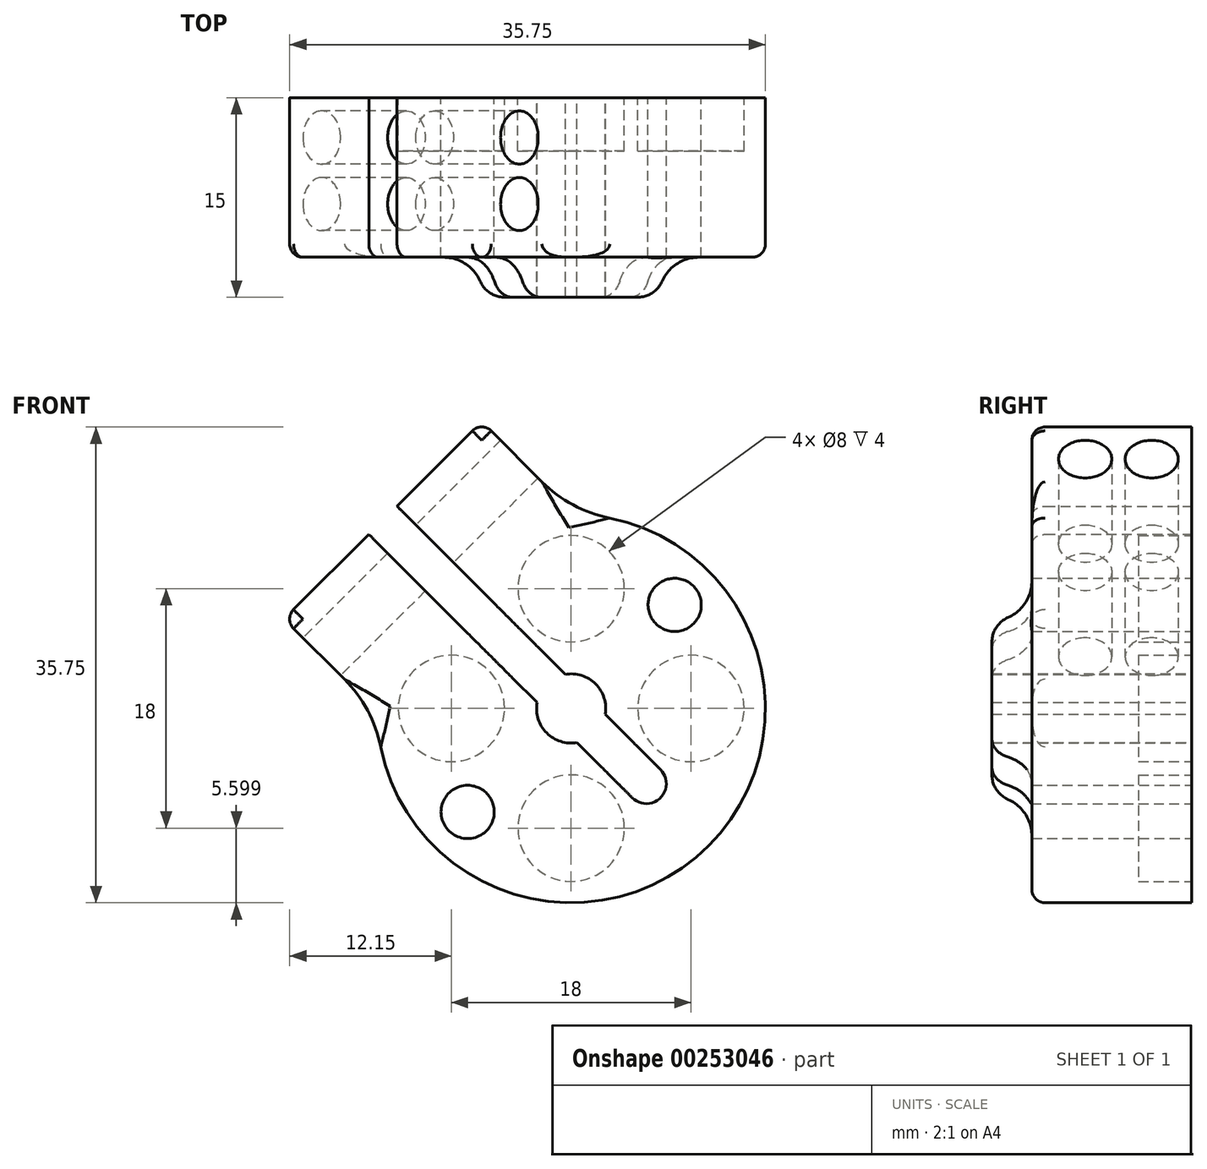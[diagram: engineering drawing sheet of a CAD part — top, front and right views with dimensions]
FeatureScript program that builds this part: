
annotation { "Feature Type Name" : "Feature", "Feature Type Description" : "" }
export const myFeature = defineFeature(function(context is Context, id is Id, definition is map)
    precondition{}
    {
        {
            var Q0;
            Q0=qCreatedBy(makeId("Right.planeOp"),FACE);
            var sketch = newSketch(context, id + "F0", { "sketchPlane" : qUnion([Q0])});
            skLineSegment(sketch, "E0", {"start": v(-60.78, -4.86) * mm, "end": v(-45.78, -4.86) * mm});
            skLineSegment(sketch, "E1", {"start": v(-45.78, -4.86) * mm, "end": v(-45.78, 7.14) * mm});
            skLineSegment(sketch, "E2", {"start": v(-45.78, 7.14) * mm, "end": v(-57.78, 7.14) * mm});
            skLineSegment(sketch, "E3", {"start": v(-57.78, 7.14) * mm, "end": v(-57.78, -0.46) * mm});
            skLineSegment(sketch, "E4", {"start": v(-57.78, -0.46) * mm, "end": v(-60.78, -0.46) * mm});
            skLineSegment(sketch, "E5", {"start": v(-60.78, -0.46) * mm, "end": v(-60.78, -4.86) * mm});
            skLineSegment(sketch, "E6", {"start": v(-43.04, -7.46) * mm, "end": v(-64.3, -7.46) * mm, "construction": true});
            skSolve(sketch);
        }
        {
            var Q0;
            Q0 = qSketchRegion(id + "F0", true);
            var Q1;
            Q1=sQuery(id+"F0.wireOp",EDGE,"E6");
            revolve(context, id + "F1", {"entities" : qUnion([Q0]), "axis" : qUnion([Q1]), "revolveType" : RevolveType.FULL});
        }
        {
            var Q0;
            Q0=makeQuery(id+"F1.opRevolve","SWEPT_EDGE",EDGE,{"disambiguationData":[OSD([sQuery(id+"F0.wireOp",EDGE,"E4"),sQuery(id+"F0.wireOp",EDGE,"E5")])]});
            fillet(context, id + "F2", {"entities" : qUnion([Q0]), "radius" : 2 * mm, "tangentPropagation" : true, "allowEdgeOverflow" : false});
        }
        {
            var Q0;
            Q0=makeQuery(id+"F1.opRevolve","SWEPT_FACE",FACE,{"disambiguationData":[OSD([sQuery(id+"F0.wireOp",EDGE,"E1")])]});
            var sketch = newSketch(context, id + "F3", { "sketchPlane" : qUnion([Q0])});
            skCircle(sketch, "E7", {"center": v(0, 1.54) * mm, "radius": 4 * mm});
            skPoint(sketch, "E8", {"position": v(0, -7.46) * mm});
            skCircle(sketch, "E9.1.0", {"center": v(-9, -7.46) * mm, "radius": 4 * mm});
            skCircle(sketch, "E9.2.0", {"center": v(0, -16.46) * mm, "radius": 4 * mm});
            skCircle(sketch, "E9.3.0", {"center": v(9, -7.46) * mm, "radius": 4 * mm});
            skSolve(sketch);
        }
        {
            var Q0;
            Q0=makeQuery(id+"F3.imprint","IMPRINT",FACE,{"disambiguationData":[TD([[makeQuery(id+"F3.imprint","IMPRINT",EDGE,{"derivedFrom":sQuery(id+"F3.wireOp",EDGE,"E7")}),1.0]])]});
            var Q1;
            Q1=makeQuery(id+"F3.imprint","IMPRINT",FACE,{"disambiguationData":[TD([[makeQuery(id+"F3.imprint","IMPRINT",EDGE,{"derivedFrom":sQuery(id+"F3.wireOp",EDGE,"E9.1.0")}),1.0]])]});
            var Q2;
            Q2=makeQuery(id+"F3.imprint","IMPRINT",FACE,{"disambiguationData":[TD([[makeQuery(id+"F3.imprint","IMPRINT",EDGE,{"derivedFrom":sQuery(id+"F3.wireOp",EDGE,"E9.2.0")}),1.0]])]});
            var Q3;
            Q3=makeQuery(id+"F3.imprint","IMPRINT",FACE,{"disambiguationData":[TD([[makeQuery(id+"F3.imprint","IMPRINT",EDGE,{"derivedFrom":sQuery(id+"F3.wireOp",EDGE,"E9.3.0")}),1.0]])]});
            extrude(context, id + "F4", {"entities" : qUnion([Q0, Q1, Q2, Q3]), "operationType" : NewBodyOperationType.REMOVE, "oppositeDirection" : true, "depth" : 4 * mm});
        }
        {
            var Q0;
            Q0=makeQuery(id+"F1.opRevolve","SWEPT_FACE",FACE,{"disambiguationData":[OSD([sQuery(id+"F0.wireOp",EDGE,"E1")])]});
            var sketch = newSketch(context, id + "F5", { "sketchPlane" : qUnion([Q0])});
            skLineSegment(sketch, "E10.0", {"start": v(0.35, -9.23) * mm, "end": v(18.03, 8.45) * mm});
            skLineSegment(sketch, "E11.0", {"start": v(-1.77, -7.1) * mm, "end": v(15.9, 10.57) * mm});
            skLineSegment(sketch, "E12", {"start": v(15.9, 10.57) * mm, "end": v(18.03, 8.45) * mm});
            skLineSegment(sketch, "E13", {"start": v(-1.77, -7.1) * mm, "end": v(0.35, -9.23) * mm});
            skPoint(sketch, "E14", {"position": v(0, -7.46) * mm});
            skSolve(sketch);
        }
        {
            var Q0;
            Q0 = qSketchRegion(id + "F5", true);
            extrude(context, id + "F6", {"entities" : qUnion([Q0]), "operationType" : NewBodyOperationType.REMOVE, "oppositeDirection" : true, "depth" : 25 * mm});
        }
        {
            var Q0;
            Q0=makeQuery(id+"F1.opRevolve","SWEPT_FACE",FACE,{"disambiguationData":[OSD([sQuery(id+"F0.wireOp",EDGE,"E1")])]});
            var sketch = newSketch(context, id + "F7", { "sketchPlane" : qUnion([Q0])});
            skPoint(sketch, "E15", {"position": v(0, -7.46) * mm});
            skLineSegment(sketch, "E16", {"start": v(8.3, 2.96) * mm, "end": v(13.08, 7.74) * mm});
            skLineSegment(sketch, "E17", {"start": v(13.08, 7.74) * mm, "end": v(6.72, 14.1) * mm});
            skLineSegment(sketch, "E18", {"start": v(6.72, 14.1) * mm, "end": v(-0.25, 7.14) * mm});
            skLineSegment(sketch, "E19", {"start": v(0, -7.46) * mm, "end": v(12.08, 4.61) * mm, "construction": true});
            skLineSegment(sketch, "E20.MirrorCS", {"start": v(15.2, 5.62) * mm, "end": v(21.57, -0.74) * mm});
            skLineSegment(sketch, "E21.MirrorCS", {"start": v(21.57, -0.74) * mm, "end": v(14.6, -7.71) * mm});
            skLineSegment(sketch, "E22.MirrorCS", {"start": v(10.42, 0.84) * mm, "end": v(15.2, 5.62) * mm});
            skLineSegment(sketch, "E23", {"start": v(-0.25, 7.14) * mm, "end": v(8.3, 2.96) * mm});
            skLineSegment(sketch, "E24", {"start": v(10.42, 0.84) * mm, "end": v(14.6, -7.71) * mm});
            skSolve(sketch);
        }
        {
            var Q0;
            Q0 = qSketchRegion(id + "F7", true);
            var Q1;
            Q1=makeQuery(id+"F1.opRevolve","SWEPT_FACE",FACE,{"disambiguationData":[OSD([sQuery(id+"F0.wireOp",EDGE,"E3")])]});
            extrude(context, id + "F8", {"entities" : qUnion([Q0]), "operationType" : NewBodyOperationType.ADD, "endBound" : BoundingType.UP_TO_SURFACE, "oppositeDirection" : true, "endBoundEntityFace" : qUnion([Q1]), "depth" : 25 * mm});
        }
        {
            var Q0;
            Q0=makeQuery(id+"F1.opRevolve","SWEPT_EDGE",EDGE,{"disambiguationData":[OSD([sQuery(id+"F0.wireOp",EDGE,"E3"),sQuery(id+"F0.wireOp",EDGE,"E4")])]});
            fillet(context, id + "F9", {"entities" : qUnion([Q0]), "radius" : 3 * mm, "tangentPropagation" : true, "allowEdgeOverflow" : false});
        }
        {
            var Q0;
            Q0=makeQuery(id+"F1.opRevolve","SWEPT_EDGE",EDGE,{"disambiguationData":[OSD([sQuery(id+"F0.wireOp",EDGE,"E2"),sQuery(id+"F0.wireOp",EDGE,"E3")])]});
            var Q1;
            Q1=makeQuery(id+"F8.opExtrude","CAP_EDGE",EDGE,{"disambiguationData":[OSD([sQuery(id+"F7.wireOp",EDGE,"E18")])],"isStart":false});
            var Q2;
            Q2=makeQuery(id+"F8.opExtrude","CAP_EDGE",EDGE,{"disambiguationData":[OSD([sQuery(id+"F7.wireOp",EDGE,"E17")])],"isStart":false});
            var Q3;
            Q3=makeQuery(id+"F8.opExtrude","CAP_EDGE",EDGE,{"disambiguationData":[OSD([sQuery(id+"F7.wireOp",EDGE,"E20.MirrorCS")])],"isStart":false});
            var Q4;
            Q4=makeQuery(id+"F8.opExtrude","CAP_EDGE",EDGE,{"disambiguationData":[OSD([sQuery(id+"F7.wireOp",EDGE,"E21.MirrorCS")])],"isStart":false});
            fillet(context, id + "F10", {"entities" : qUnion([Q0, Q1, Q2, Q3, Q4]), "radius" : 1 * mm, "tangentPropagation" : true, "allowEdgeOverflow" : false});
        }
        {
            var Q0;
            Q0=makeQuery(id+"F8.boolean.opBoolean","INTERSECT",EDGE,{"derivedFrom":[makeQuery(id+"F1.opRevolve","SWEPT_FACE",FACE,{"disambiguationData":[OSD([sQuery(id+"F0.wireOp",EDGE,"E2")])]}),makeQuery(id+"F8.opExtrude","SWEPT_FACE",FACE,{"disambiguationData":[OSD([sQuery(id+"F7.wireOp",EDGE,"E18")])]})]});
            var Q1;
            Q1=makeQuery(id+"F8.boolean.opBoolean","INTERSECT",EDGE,{"derivedFrom":[makeQuery(id+"F1.opRevolve","SWEPT_FACE",FACE,{"disambiguationData":[OSD([sQuery(id+"F0.wireOp",EDGE,"E2")])]}),makeQuery(id+"F8.opExtrude","SWEPT_FACE",FACE,{"disambiguationData":[OSD([sQuery(id+"F7.wireOp",EDGE,"E21.MirrorCS")])]})]});
            var Q2;
            Q2=makeQuery(id+"F10.opFillet","BLEND_EDGE",EDGE,{"blendedFrom":[makeQuery(id+"F8.opExtrude","CAP_EDGE",EDGE,{"disambiguationData":[OSD([sQuery(id+"F7.wireOp",EDGE,"E18")])],"isStart":false}),makeQuery(id+"F1.opRevolve","SWEPT_EDGE",EDGE,{"disambiguationData":[OSD([sQuery(id+"F0.wireOp",EDGE,"E2"),sQuery(id+"F0.wireOp",EDGE,"E3")])]})],"blendedInto":[]});
            var Q3;
            Q3=makeQuery(id+"F10.opFillet","BLEND_EDGE",EDGE,{"blendedFrom":[makeQuery(id+"F8.opExtrude","CAP_EDGE",EDGE,{"disambiguationData":[OSD([sQuery(id+"F7.wireOp",EDGE,"E21.MirrorCS")])],"isStart":false}),makeQuery(id+"F1.opRevolve","SWEPT_EDGE",EDGE,{"disambiguationData":[OSD([sQuery(id+"F0.wireOp",EDGE,"E2"),sQuery(id+"F0.wireOp",EDGE,"E3")])]})],"blendedInto":[]});
            fillet(context, id + "F11", {"entities" : qUnion([Q0, Q1, Q2, Q3]), "radius" : 10 * mm, "tangentPropagation" : true, "allowEdgeOverflow" : false});
        }
        {
            var Q0;
            Q0=makeQuery(id+"F10.opFillet","BLEND_EDGE",EDGE,{"blendedFrom":[makeQuery(id+"F8.opExtrude","CAP_EDGE",EDGE,{"disambiguationData":[OSD([sQuery(id+"F7.wireOp",EDGE,"E17")])],"isStart":false}),makeQuery(id+"F8.opExtrude","CAP_EDGE",EDGE,{"disambiguationData":[OSD([sQuery(id+"F7.wireOp",EDGE,"E18")])],"isStart":false})],"blendedInto":[]});
            var Q1;
            Q1=makeQuery(id+"F10.opFillet","BLEND_EDGE",EDGE,{"blendedFrom":[makeQuery(id+"F8.opExtrude","CAP_EDGE",EDGE,{"disambiguationData":[OSD([sQuery(id+"F7.wireOp",EDGE,"E20.MirrorCS")])],"isStart":false}),makeQuery(id+"F8.opExtrude","CAP_EDGE",EDGE,{"disambiguationData":[OSD([sQuery(id+"F7.wireOp",EDGE,"E21.MirrorCS")])],"isStart":false})],"blendedInto":[]});
            var Q2;
            Q2=makeQuery(id+"F8.opExtrude","SWEPT_EDGE",EDGE,{"disambiguationData":[OSD([sQuery(id+"F7.wireOp",EDGE,"E20.MirrorCS"),sQuery(id+"F7.wireOp",EDGE,"E21.MirrorCS")])]});
            var Q3;
            {var subQ0=sQuery(id+"F0.wireOp",EDGE,"E3");Q3=makeQuery(id+"F10.opFillet","BLEND_EDGE",EDGE,{"blendedFrom":[makeQuery(id+"F1.opRevolve","SWEPT_EDGE",EDGE,{"disambiguationData":[OSD([sQuery(id+"F0.wireOp",EDGE,"E2"),subQ0])]}),makeQuery(id+"F8.boolean.opBoolean","MERGE",FACE,{"derivedFrom":[makeQuery(id+"F1.opRevolve","SWEPT_FACE",FACE,{"disambiguationData":[OSD([subQ0])]}),makeQuery(id+"F8.opExtrude","CAP_FACE",FACE,{"disambiguationData":[OSD([sQuery(id+"F7.wireOp",EDGE,"E16"),sQuery(id+"F7.wireOp",EDGE,"E17"),sQuery(id+"F7.wireOp",EDGE,"E18"),sQuery(id+"F7.wireOp",EDGE,"E23")])],"isStart":false}),makeQuery(id+"F8.opExtrude","CAP_FACE",FACE,{"disambiguationData":[OSD([sQuery(id+"F7.wireOp",EDGE,"E20.MirrorCS"),sQuery(id+"F7.wireOp",EDGE,"E21.MirrorCS"),sQuery(id+"F7.wireOp",EDGE,"E22.MirrorCS"),sQuery(id+"F7.wireOp",EDGE,"E24")])],"isStart":false})]})],"blendedInto":[makeQuery(id+"F8.boolean.opBoolean","MERGE",FACE,{"derivedFrom":[makeQuery(id+"F1.opRevolve","SWEPT_FACE",FACE,{"disambiguationData":[OSD([subQ0])]}),makeQuery(id+"F8.opExtrude","CAP_FACE",FACE,{"disambiguationData":[OSD([sQuery(id+"F7.wireOp",EDGE,"E16"),sQuery(id+"F7.wireOp",EDGE,"E17"),sQuery(id+"F7.wireOp",EDGE,"E18"),sQuery(id+"F7.wireOp",EDGE,"E23")])],"isStart":false}),makeQuery(id+"F8.opExtrude","CAP_FACE",FACE,{"disambiguationData":[OSD([sQuery(id+"F7.wireOp",EDGE,"E20.MirrorCS"),sQuery(id+"F7.wireOp",EDGE,"E21.MirrorCS"),sQuery(id+"F7.wireOp",EDGE,"E22.MirrorCS"),sQuery(id+"F7.wireOp",EDGE,"E24")])],"isStart":false})]})]});}
            var Q4;
            {var subQ0=sQuery(id+"F7.wireOp",EDGE,"E18");Q4=makeQuery(id+"F10.opFillet","BLEND_EDGE",EDGE,{"blendedFrom":[makeQuery(id+"F8.opExtrude","CAP_EDGE",EDGE,{"disambiguationData":[OSD([subQ0])],"isStart":false}),makeQuery(id+"F8.boolean.opBoolean","MERGE",FACE,{"derivedFrom":[makeQuery(id+"F1.opRevolve","SWEPT_FACE",FACE,{"disambiguationData":[OSD([sQuery(id+"F0.wireOp",EDGE,"E3")])]}),makeQuery(id+"F8.opExtrude","CAP_FACE",FACE,{"disambiguationData":[OSD([sQuery(id+"F7.wireOp",EDGE,"E16"),sQuery(id+"F7.wireOp",EDGE,"E17"),subQ0,sQuery(id+"F7.wireOp",EDGE,"E23")])],"isStart":false}),makeQuery(id+"F8.opExtrude","CAP_FACE",FACE,{"disambiguationData":[OSD([sQuery(id+"F7.wireOp",EDGE,"E20.MirrorCS"),sQuery(id+"F7.wireOp",EDGE,"E21.MirrorCS"),sQuery(id+"F7.wireOp",EDGE,"E22.MirrorCS"),sQuery(id+"F7.wireOp",EDGE,"E24")])],"isStart":false})]})],"blendedInto":[makeQuery(id+"F8.boolean.opBoolean","MERGE",FACE,{"derivedFrom":[makeQuery(id+"F1.opRevolve","SWEPT_FACE",FACE,{"disambiguationData":[OSD([sQuery(id+"F0.wireOp",EDGE,"E3")])]}),makeQuery(id+"F8.opExtrude","CAP_FACE",FACE,{"disambiguationData":[OSD([sQuery(id+"F7.wireOp",EDGE,"E16"),sQuery(id+"F7.wireOp",EDGE,"E17"),subQ0,sQuery(id+"F7.wireOp",EDGE,"E23")])],"isStart":false}),makeQuery(id+"F8.opExtrude","CAP_FACE",FACE,{"disambiguationData":[OSD([sQuery(id+"F7.wireOp",EDGE,"E20.MirrorCS"),sQuery(id+"F7.wireOp",EDGE,"E21.MirrorCS"),sQuery(id+"F7.wireOp",EDGE,"E22.MirrorCS"),sQuery(id+"F7.wireOp",EDGE,"E24")])],"isStart":false})]})]});}
            var Q5;
            {var subQ0=sQuery(id+"F7.wireOp",EDGE,"E21.MirrorCS");Q5=makeQuery(id+"F10.opFillet","BLEND_EDGE",EDGE,{"blendedFrom":[makeQuery(id+"F8.opExtrude","CAP_EDGE",EDGE,{"disambiguationData":[OSD([subQ0])],"isStart":false}),makeQuery(id+"F8.boolean.opBoolean","MERGE",FACE,{"derivedFrom":[makeQuery(id+"F1.opRevolve","SWEPT_FACE",FACE,{"disambiguationData":[OSD([sQuery(id+"F0.wireOp",EDGE,"E3")])]}),makeQuery(id+"F8.opExtrude","CAP_FACE",FACE,{"disambiguationData":[OSD([sQuery(id+"F7.wireOp",EDGE,"E16"),sQuery(id+"F7.wireOp",EDGE,"E17"),sQuery(id+"F7.wireOp",EDGE,"E18"),sQuery(id+"F7.wireOp",EDGE,"E23")])],"isStart":false}),makeQuery(id+"F8.opExtrude","CAP_FACE",FACE,{"disambiguationData":[OSD([sQuery(id+"F7.wireOp",EDGE,"E20.MirrorCS"),subQ0,sQuery(id+"F7.wireOp",EDGE,"E22.MirrorCS"),sQuery(id+"F7.wireOp",EDGE,"E24")])],"isStart":false})]})],"blendedInto":[makeQuery(id+"F8.boolean.opBoolean","MERGE",FACE,{"derivedFrom":[makeQuery(id+"F1.opRevolve","SWEPT_FACE",FACE,{"disambiguationData":[OSD([sQuery(id+"F0.wireOp",EDGE,"E3")])]}),makeQuery(id+"F8.opExtrude","CAP_FACE",FACE,{"disambiguationData":[OSD([sQuery(id+"F7.wireOp",EDGE,"E16"),sQuery(id+"F7.wireOp",EDGE,"E17"),sQuery(id+"F7.wireOp",EDGE,"E18"),sQuery(id+"F7.wireOp",EDGE,"E23")])],"isStart":false}),makeQuery(id+"F8.opExtrude","CAP_FACE",FACE,{"disambiguationData":[OSD([sQuery(id+"F7.wireOp",EDGE,"E20.MirrorCS"),subQ0,sQuery(id+"F7.wireOp",EDGE,"E22.MirrorCS"),sQuery(id+"F7.wireOp",EDGE,"E24")])],"isStart":false})]})]});}
            fillet(context, id + "F12", {"entities" : qUnion([Q0, Q1, Q2, Q3, Q4, Q5]), "radius" : 1 * mm, "tangentPropagation" : true, "allowEdgeOverflow" : false});
        }
        {
            var Q0;
            Q0=makeQuery(id+"F8.opExtrude","SWEPT_FACE",FACE,{"disambiguationData":[OSD([sQuery(id+"F7.wireOp",EDGE,"E21.MirrorCS")])]});
            var sketch = newSketch(context, id + "F13", { "sketchPlane" : qUnion([Q0])});
            skCircle(sketch, "E25", {"center": v(48.78, 10.72) * mm, "radius": 2 * mm});
            skLineSegment(sketch, "E26", {"start": v(51.28, 13.72) * mm, "end": v(51.28, 6.7) * mm, "construction": true});
            skCircle(sketch, "E27.MirrorC", {"center": v(53.78, 10.72) * mm, "radius": 2 * mm});
            skSolve(sketch);
        }
        {
            var Q0;
            Q0 = qSketchRegion(id + "F13", true);
            extrude(context, id + "F14", {"entities" : qUnion([Q0]), "operationType" : NewBodyOperationType.REMOVE, "endBound" : BoundingType.SYMMETRIC, "oppositeDirection" : true, "depth" : 50 * mm});
        }
        {
            var Q0;
            Q0=makeQuery(id+"F8.boolean.opBoolean","MERGE",FACE,{"derivedFrom":[makeQuery(id+"F1.opRevolve","SWEPT_FACE",FACE,{"disambiguationData":[OSD([sQuery(id+"F0.wireOp",EDGE,"E1")])]}),makeQuery(id+"F8.opExtrude","CAP_FACE",FACE,{"disambiguationData":[OSD([sQuery(id+"F7.wireOp",EDGE,"E16"),sQuery(id+"F7.wireOp",EDGE,"E17"),sQuery(id+"F7.wireOp",EDGE,"E18"),sQuery(id+"F7.wireOp",EDGE,"E23")])],"isStart":true}),makeQuery(id+"F8.opExtrude","CAP_FACE",FACE,{"disambiguationData":[OSD([sQuery(id+"F7.wireOp",EDGE,"E20.MirrorCS"),sQuery(id+"F7.wireOp",EDGE,"E21.MirrorCS"),sQuery(id+"F7.wireOp",EDGE,"E22.MirrorCS"),sQuery(id+"F7.wireOp",EDGE,"E24")])],"isStart":true})]});
            var sketch = newSketch(context, id + "F15", { "sketchPlane" : qUnion([Q0])});
            skPoint(sketch, "E28", {"position": v(0, -7.46) * mm});
            skLineSegment(sketch, "E29", {"start": v(0, -7.46) * mm, "end": v(-5.66, -13.12) * mm, "construction": true});
            skLineSegment(sketch, "E30.0", {"start": v(1.06, -8.52) * mm, "end": v(-4.6, -14.18) * mm});
            skLineSegment(sketch, "E31.0", {"start": v(-1.06, -6.4) * mm, "end": v(-6.72, -12.06) * mm});
            skArc(sketch, "E32", {"start": v(-6.72, -12.06) * mm, "mid": v(-6.72, -14.18) * mm, "end": v(-4.6, -14.18) * mm});
            skLineSegment(sketch, "E33", {"start": v(-1.06, -6.4) * mm, "end": v(1.06, -8.52) * mm});
            skLineSegment(sketch, "E34", {"start": v(-4.6, -14.18) * mm, "end": v(-6.72, -12.06) * mm, "construction": true});
            skSolve(sketch);
        }
        {
            var Q0;
            Q0 = qSketchRegion(id + "F15", true);
            extrude(context, id + "F16", {"entities" : qUnion([Q0]), "operationType" : NewBodyOperationType.REMOVE, "oppositeDirection" : true, "depth" : 25 * mm});
        }
        {
            var Q0;
            Q0=makeQuery(id+"F8.boolean.opBoolean","MERGE",FACE,{"derivedFrom":[makeQuery(id+"F1.opRevolve","SWEPT_FACE",FACE,{"disambiguationData":[OSD([sQuery(id+"F0.wireOp",EDGE,"E1")])]}),makeQuery(id+"F8.opExtrude","CAP_FACE",FACE,{"disambiguationData":[OSD([sQuery(id+"F7.wireOp",EDGE,"E16"),sQuery(id+"F7.wireOp",EDGE,"E17"),sQuery(id+"F7.wireOp",EDGE,"E18"),sQuery(id+"F7.wireOp",EDGE,"E23")])],"isStart":true}),makeQuery(id+"F8.opExtrude","CAP_FACE",FACE,{"disambiguationData":[OSD([sQuery(id+"F7.wireOp",EDGE,"E20.MirrorCS"),sQuery(id+"F7.wireOp",EDGE,"E21.MirrorCS"),sQuery(id+"F7.wireOp",EDGE,"E22.MirrorCS"),sQuery(id+"F7.wireOp",EDGE,"E24")])],"isStart":true})]});
            var sketch = newSketch(context, id + "F17", { "sketchPlane" : qUnion([Q0])});
            skLineSegment(sketch, "E35", {"start": v(0, -7.46) * mm, "end": v(-7.78, 0.32) * mm, "construction": true});
            skCircle(sketch, "E36", {"center": v(-7.78, 0.32) * mm, "radius": 2 * mm});
            skLineSegment(sketch, "E37", {"start": v(0, -7.46) * mm, "end": v(14.34, 6.88) * mm, "construction": true});
            skCircle(sketch, "E38.MirrorC", {"center": v(7.78, -15.24) * mm, "radius": 2 * mm});
            skSolve(sketch);
        }
        {
            var Q0;
            Q0 = qSketchRegion(id + "F17", true);
            extrude(context, id + "F18", {"entities" : qUnion([Q0]), "operationType" : NewBodyOperationType.REMOVE, "endBound" : BoundingType.SYMMETRIC, "oppositeDirection" : true, "depth" : 25 * mm});
        }
    });
